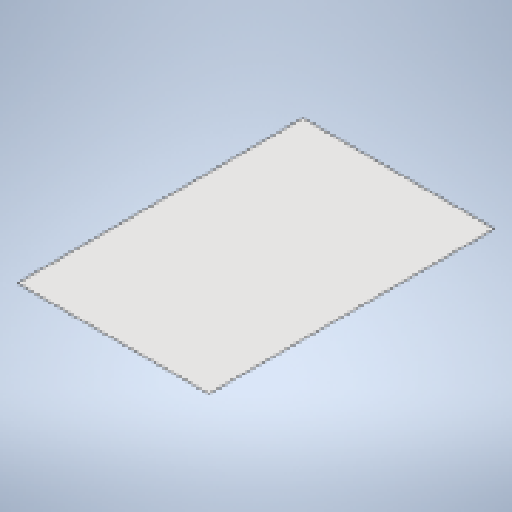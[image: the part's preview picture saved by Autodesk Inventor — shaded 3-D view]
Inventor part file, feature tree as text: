
AUTODESK INVENTOR PART (.ipt)
format: ipt  version: 2025 (Build 290162010, 162A)  size: 160,256 bytes
history: native  units: mm
features: other x2, sheet_metal_op x1, sketch x1
ambient origin geometry x8: Origin, YZ Plane, XZ Plane, XY Plane, X Axis, Y Axis, Z Axis, Center Point
bodies: Solid1 (feature_tree)
feature tree (4):
  sheet_metal_op  "Face1"
  sketch  "Sketch1"  dims[d0=2000.0mm d1=2980.0mm d2=3.0mm]
  other  "Plate1"
  other  "Definition1"
